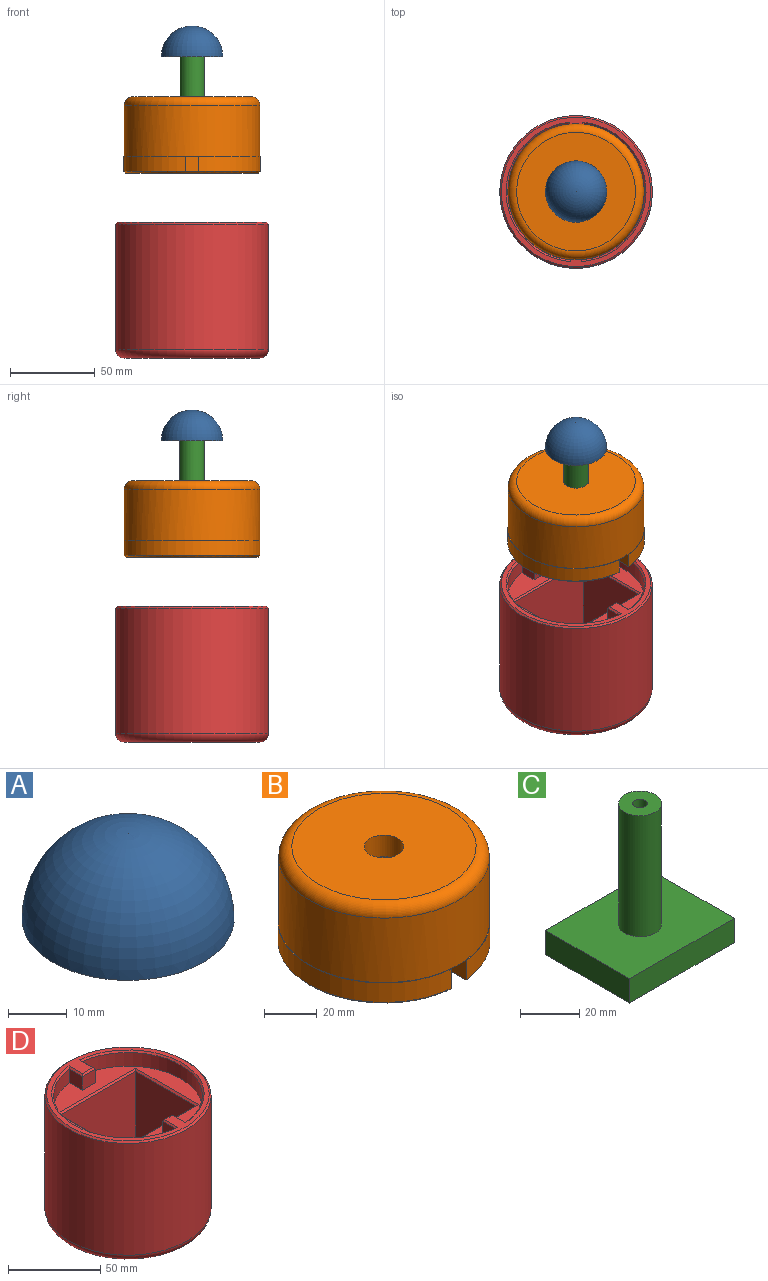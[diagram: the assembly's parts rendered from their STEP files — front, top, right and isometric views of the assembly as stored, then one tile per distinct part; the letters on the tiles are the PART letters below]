
ASSEMBLY  parts=4 mates=3
PART A: 4 faces, bbox 36.2x36.2x25 mm
  f0: torus R=0.09mm, axis (0,0,1), area 2051.4mm2, adj f1
  f1: plane 36.18x36.18mm, normal (0,0,-1), area 988.5mm2, adj f0,f2
  f2: cylinder r=3.54mm len=7.08mm, axis (0,0,1), area 156.7mm2, adj f1,f3
  f3: plane 7.08x7.08mm, normal (0,0,-1), area 39.3mm2, adj f2
PART B: 35 faces, bbox 86.6x86.6x45 mm
  f0: plane 58x46mm, normal (0,0,-1), area 292mm2, adj f2,f3,f4,f5,f20,f21,f22,f23
  f1: plane 10.06x10mm, normal (0,0,-1), area 99.6mm2, adj f6,f13,f19,f24
  f2: plane 44x25mm, normal (1,0,0), area 1100mm2, adj f0,f3,f5,f10
  f3: plane 54x25mm, normal (0,-1,0), area 1350mm2, adj f0,f2,f4,f10
  f4: plane 44x25mm, normal (-1,0,0), area 1100mm2, adj f0,f3,f5,f10
  f5: plane 54x25mm, normal (0,1,0), area 1350mm2, adj f0,f2,f4,f10
  f6: cylinder r=40mm len=80mm, axis (0,0,1), area 7539.8mm2, adj f1,f7,f11,f12,f34
  f7: plane 9.95x8mm, normal (0,0,-1), area 79.1mm2, adj f6,f15,f16,f17
  f8: cylinder r=7.5mm len=15mm, axis (0,0,-1), area 471.2mm2, adj f9,f10
  f9: plane 70x70mm, normal (0,0,1), area 3671.7mm2, adj f8,f34
  f10: plane 54x44mm, normal (0,0,-1), area 2199.3mm2, adj f2,f3,f4,f5,f8
  f11: plane 79.99x36.25mm, normal (0,0,1), area 29.3mm2, adj f6,f13,f14,f15
  f12: plane 79.99x36.25mm, normal (0,0,1), area 29.3mm2, adj f6,f17,f18,f19
  f13: plane 10x9mm, normal (1,0,0), area 90mm2, adj f1,f11,f14,f24,f33
  f14: cylinder r=40.25mm len=79.99mm, axis (0,0,1), area 1056.9mm2, adj f11,f13,f15,f31
  f15: plane 10x9mm, normal (1,0,0), area 90mm2, adj f7,f11,f14,f16,f29
  f16: plane 9x8mm, normal (0,-1,0), area 72mm2, adj f7,f15,f17,f27
  f17: plane 10x9mm, normal (-1,0,0), area 90mm2, adj f7,f12,f16,f18,f26
  f18: cylinder r=40.25mm len=79.99mm, axis (0,0,1), area 1056.9mm2, adj f12,f17,f19,f28
  f19: plane 10x9mm, normal (-1,0,0), area 90mm2, adj f1,f12,f18,f24,f30
  f20: plane 46x10mm, normal (1,0,0), area 460mm2, adj f0,f21,f23,f25
  f21: plane 58x10mm, normal (0,-1,0), area 580mm2, adj f0,f20,f22,f25
  f22: plane 46x10mm, normal (-1,0,0), area 460mm2, adj f0,f21,f23,f25
  f23: plane 58x10mm, normal (0,1,0), area 580mm2, adj f0,f20,f22,f25
  f24: plane 10x9mm, normal (0,1,0), area 90mm2, adj f1,f13,f19,f32
  f25: plane 78.5x77.72mm, normal (0,0,-1), area 1949mm2, adj f20,f21,f22,f23,f26,f27,f28,f29
  f26: plane 11.01x1.01mm, normal (-0.71,0,-0.71), area 14.1mm2, adj f17,f25,f27,f28
  f27: plane 10x1mm, normal (0,-0.71,-0.71), area 12.7mm2, adj f16,f25,f26,f29
  f28: cone r=40.25mm half-angle=45deg, axis (0,0,1), area 162.4mm2, adj f18,f25,f26,f30
  f29: plane 11.01x1.01mm, normal (0.71,0,-0.71), area 14.1mm2, adj f15,f25,f27,f31
  f30: plane 11.01x1.01mm, normal (-0.71,0,-0.71), area 14mm2, adj f19,f25,f28,f32
  f31: cone r=40.25mm half-angle=45deg, axis (0,0,1), area 162.4mm2, adj f14,f25,f29,f33
  f32: plane 12x1mm, normal (0,0.71,-0.71), area 15.6mm2, adj f24,f25,f30,f33
  f33: plane 11.01x1.01mm, normal (0.71,0,-0.71), area 14mm2, adj f13,f25,f31,f32
  f34: torus R=35mm, axis (0,0,1), area 1884.3mm2, adj f6,f9
PART C: 10 faces, bbox 50x40x60 mm
  f0: cylinder r=7.25mm len=50mm, axis (0,0,1), area 2277.7mm2, adj f1,f7
  f1: plane 14.5x14.5mm, normal (0,0,1), area 145.5mm2, adj f0,f9
  f2: plane 40x10mm, normal (1,0,0), area 400mm2, adj f3,f5,f6,f7
  f3: plane 50x10mm, normal (0,-1,0), area 500mm2, adj f2,f4,f6,f7
  f4: plane 40x10mm, normal (-1,0,0), area 400mm2, adj f3,f5,f6,f7
  f5: plane 50x10mm, normal (0,1,0), area 500mm2, adj f2,f4,f6,f7
  f6: plane 50x40mm, normal (0,0,-1), area 2000mm2, adj f2,f3,f4,f5
  f7: plane 50x40mm, normal (0,0,1), area 1834.9mm2, adj f0,f2,f3,f4,f5
  f8: cone r=0mm half-angle=59deg, axis (0,0,1), area 22.9mm2, adj f9
  f9: cylinder r=2.5mm len=8mm, axis (0,0,1), area 125.7mm2, adj f1,f8
PART D: 31 faces, bbox 97.4x97.4x80 mm
  f0: plane 88x88mm, normal (0,0,1), area 879.5mm2, adj f17,f22,f23,f24,f25,f26,f27,f28
  f1: cylinder r=45mm len=90mm, axis (0,0,1), area 20923mm2, adj f17,f30
  f2: plane 80x80mm, normal (0,0,-1), area 5026.5mm2, adj f30
  f3: plane 10x9mm, normal (-1,0,0), area 90mm2, adj f4,f10,f11,f27
  f4: cylinder r=40.25mm len=79.99mm, axis (0,0,1), area 1056.9mm2, adj f3,f5,f11,f29
  f5: plane 10x9mm, normal (-1,0,0), area 90mm2, adj f4,f6,f11,f28
  f6: plane 9x8mm, normal (0,1,0), area 72mm2, adj f5,f7,f11,f26
  f7: plane 10x9mm, normal (1,0,0), area 90mm2, adj f6,f8,f11,f24
  f8: cylinder r=40.25mm len=79.99mm, axis (0,0,1), area 1056.9mm2, adj f7,f9,f11,f22
  f9: plane 10x9mm, normal (1,0,0), area 90mm2, adj f8,f10,f11,f23
  f10: plane 10x9mm, normal (0,-1,0), area 90mm2, adj f3,f9,f11,f25
  f11: plane 80.5x79.99mm, normal (0,0,1), area 2026.4mm2, adj f3,f4,f5,f6,f7,f8,f9,f10
  f12: plane 58x46mm, normal (0,0,1), area 2668mm2, adj f13,f14,f15,f16
  f13: plane 49x46mm, normal (-1,0,0), area 2254mm2, adj f12,f14,f16,f18
  f14: plane 58x49mm, normal (0,1,0), area 2842mm2, adj f12,f13,f15,f19
  f15: plane 49x46mm, normal (1,0,0), area 2254mm2, adj f12,f14,f16,f21
  f16: plane 58x49mm, normal (0,-1,0), area 2842mm2, adj f12,f13,f15,f20
  f17: cone r=45mm half-angle=45deg, axis (0,0,-1), area 395.4mm2, adj f0,f1
  f18: plane 48x1mm, normal (-0.71,0,0.71), area 66.5mm2, adj f11,f13,f19,f20
  f19: plane 60x1mm, normal (0,0.71,0.71), area 83.4mm2, adj f11,f14,f18,f21
  f20: plane 60x1mm, normal (0,-0.71,0.71), area 83.4mm2, adj f11,f16,f18,f21
  f21: plane 48x1mm, normal (0.71,0,0.71), area 66.5mm2, adj f11,f15,f19,f20
  f22: cone r=40.25mm half-angle=45deg, axis (0,0,1), area 169.7mm2, adj f0,f8,f23,f24
  f23: plane 11.13x1.01mm, normal (0.71,0,0.71), area 14.2mm2, adj f0,f9,f22,f25
  f24: plane 11.1x1.01mm, normal (0.71,0,0.71), area 14.2mm2, adj f0,f7,f22,f26
  f25: plane 10x1mm, normal (0,-0.71,0.71), area 12.7mm2, adj f0,f10,f23,f27
  f26: plane 8x1mm, normal (0,0.71,0.71), area 9.9mm2, adj f0,f6,f24,f28
  f27: plane 11.13x1.01mm, normal (-0.71,0,0.71), area 14.2mm2, adj f0,f3,f25,f29
  f28: plane 11.1x1.01mm, normal (-0.71,0,0.71), area 14.2mm2, adj f0,f5,f26,f29
  f29: cone r=40.25mm half-angle=45deg, axis (0,0,1), area 169.7mm2, adj f0,f4,f27,f28
  f30: torus R=40mm, axis (0,0,-1), area 2131mm2, adj f1,f2
PLACE A t=(42.93,-45.67,50.78)mm
PLACE B t=(42.93,-45.58,67.01)mm fixed
PLACE C t=(42.93,-45.58,50.78)mm
PLACE D t=(42.93,-45.58,28.01)mm
MATE slider D.f4 <-> B.f18  axis (0,0,1) through (42.93,-45.58,-52.49)mm
MATE slider C.f0 <-> B.f8  axis (0,0,1) through (42.93,-45.58,50.78)mm
MATE fastened C.f0 <-> A.f2  axis (0,0,1) through (42.93,-45.58,50.78)mm
